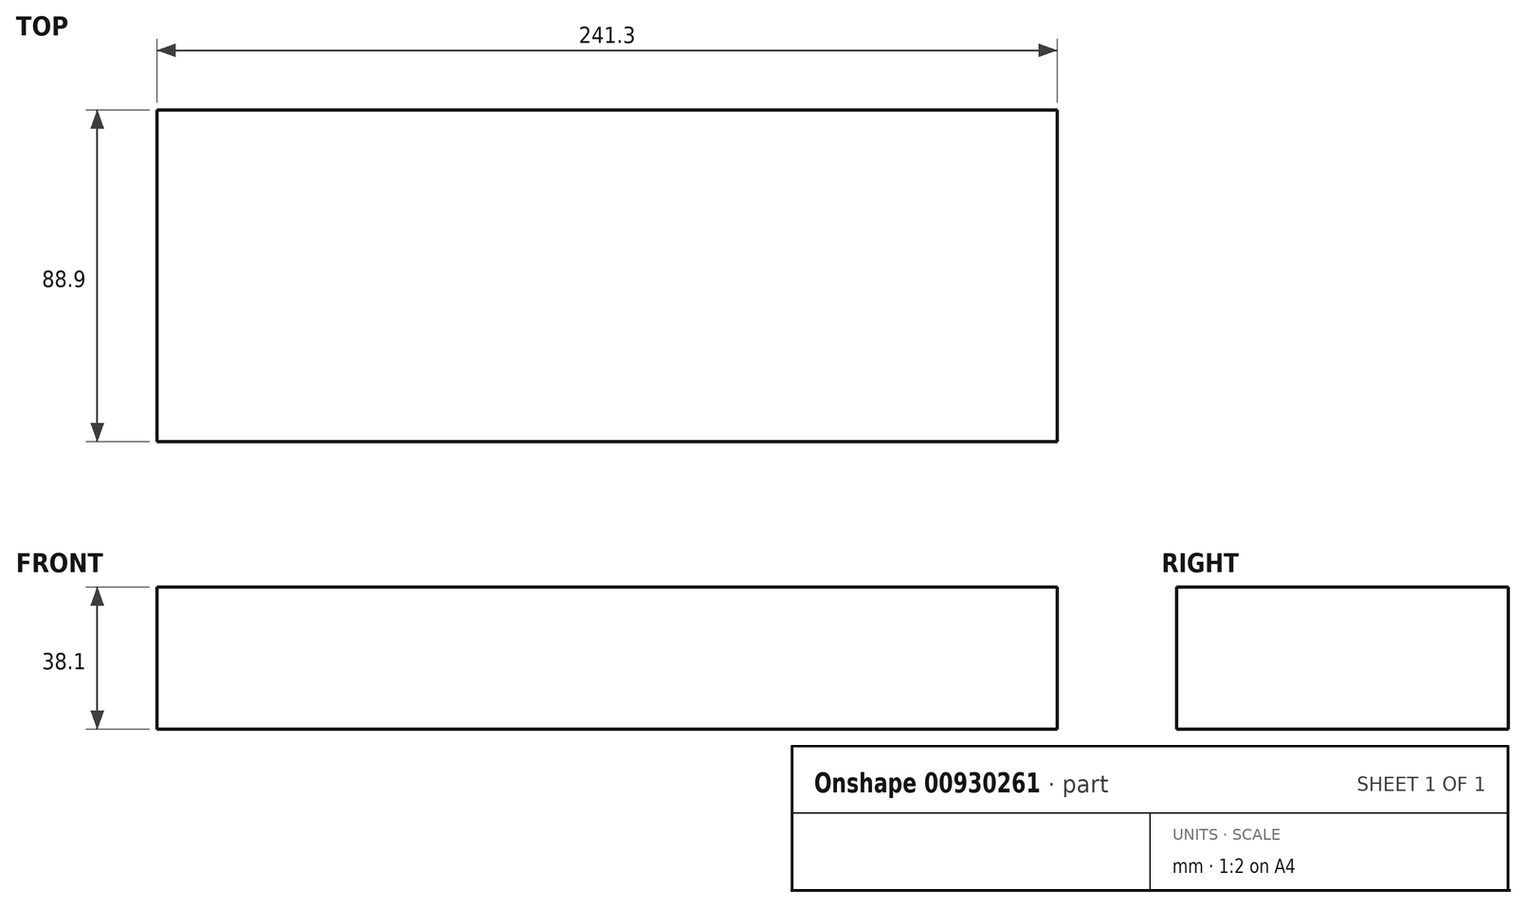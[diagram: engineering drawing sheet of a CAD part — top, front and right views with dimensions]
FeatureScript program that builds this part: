
annotation { "Feature Type Name" : "Feature", "Feature Type Description" : "" }
export const myFeature = defineFeature(function(context is Context, id is Id, definition is map)
    precondition{}
    {
        {
            var Q0;
            Q0=qCreatedBy(makeId("Right.planeOp"),FACE);
            var sketch = newSketch(context, id + "F0", { "sketchPlane" : qUnion([Q0])});
            skLineSegment(sketch, "E0.bottom", {"start": v(44.45, -19.05) * mm, "end": v(-44.45, -19.05) * mm});
            skLineSegment(sketch, "E0.top", {"start": v(44.45, 19.05) * mm, "end": v(-44.45, 19.05) * mm});
            skLineSegment(sketch, "E0.left", {"start": v(44.45, -19.05) * mm, "end": v(44.45, 19.05) * mm});
            skLineSegment(sketch, "E0.right", {"start": v(-44.45, -19.05) * mm, "end": v(-44.45, 19.05) * mm});
            skPoint(sketch, "E0.middle", {"position": v(0, 0) * mm});
            skSolve(sketch);
        }
        {
            var Q0;
            Q0=qSketchRegion(id+"F0",true);
            extrude(context, id + "F1", {"entities" : qUnion([Q0]), "endBound" : BoundingType.SYMMETRIC, "depth" : 241.3 * mm});
        }
    });
